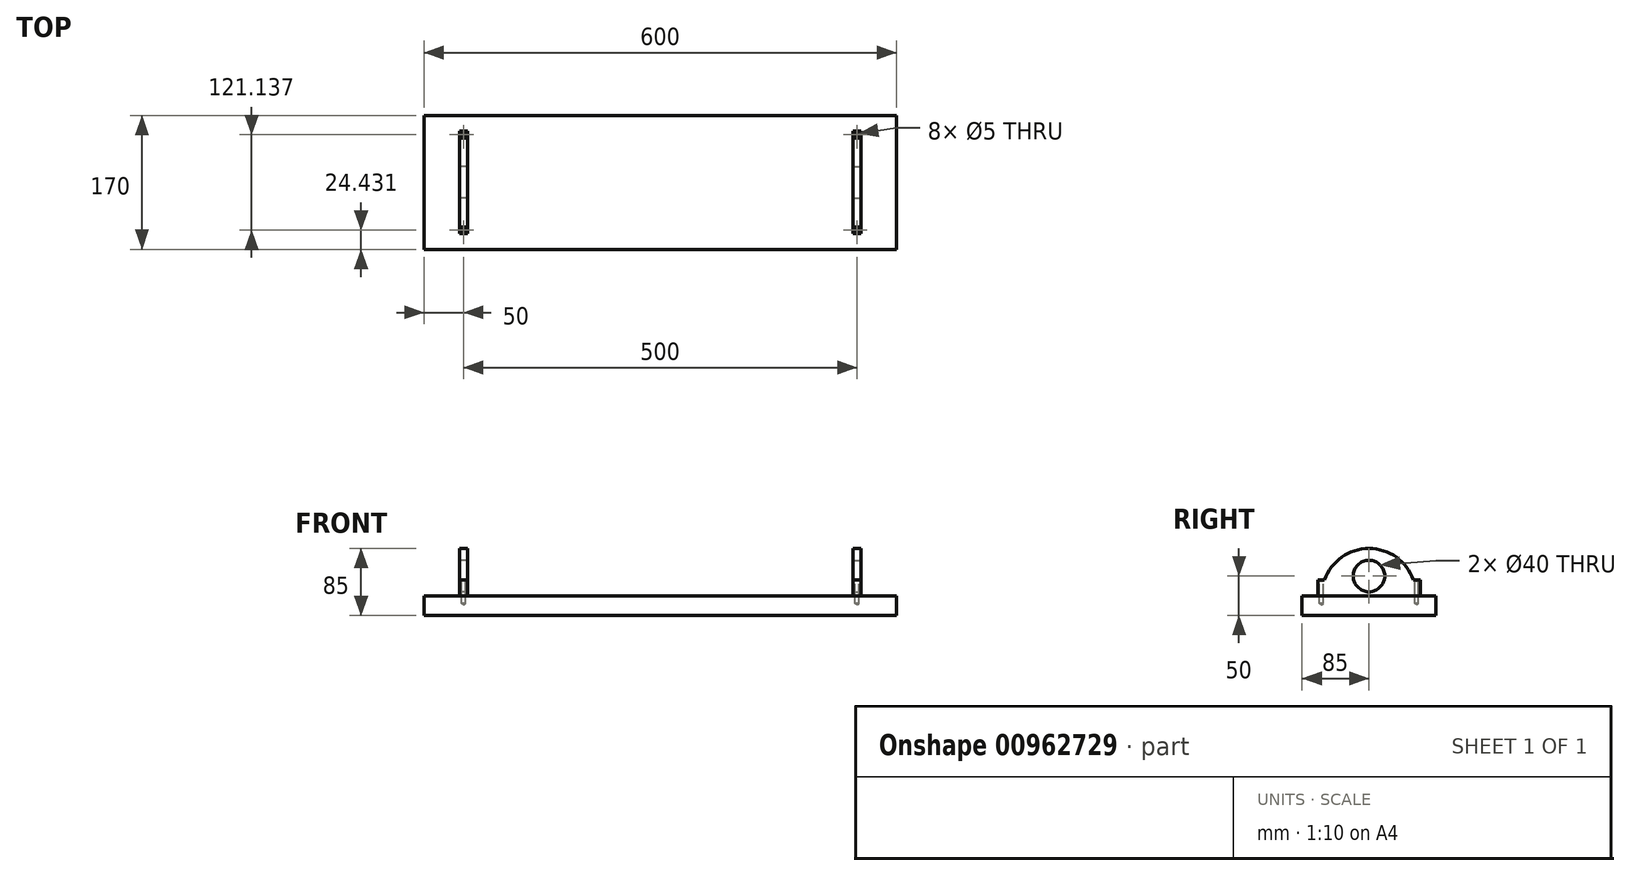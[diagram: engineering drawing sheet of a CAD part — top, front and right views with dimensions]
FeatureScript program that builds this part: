
annotation { "Feature Type Name" : "Feature", "Feature Type Description" : "" }
export const myFeature = defineFeature(function(context is Context, id is Id, definition is map)
    precondition{}
    {
        {
            var Q0;
            Q0=qCreatedBy(makeId("Top.planeOp"),FACE);
            var sketch = newSketch(context, id + "F0", { "sketchPlane" : qUnion([Q0])});
            skLineSegment(sketch, "E0.bottom", {"start": v(300, -85) * mm, "end": v(-300, -85) * mm});
            skLineSegment(sketch, "E0.top", {"start": v(300, 85) * mm, "end": v(-300, 85) * mm});
            skLineSegment(sketch, "E0.left", {"start": v(300, -85) * mm, "end": v(300, 85) * mm});
            skLineSegment(sketch, "E0.right", {"start": v(-300, -85) * mm, "end": v(-300, 85) * mm});
            skPoint(sketch, "E0.middle", {"position": v(0, 0) * mm});
            skSolve(sketch);
        }
        {
            var Q0;
            Q0=qSketchRegion(id+"F0",true);
            extrude(context, id + "F1", {"entities" : qUnion([Q0]), "depth" : 25 * mm, "offsetDistance" : 25 * mm});
        }
        {
            var Q0;
            Q0=qCreatedBy(makeId("Right.planeOp"),FACE);
            var sketch = newSketch(context, id + "F2", { "sketchPlane" : qUnion([Q0])});
            skLineSegment(sketch, "E1", {"start": v(65, 25) * mm, "end": v(65, 45) * mm});
            skLineSegment(sketch, "E2", {"start": v(65, 45) * mm, "end": v(56.57, 45) * mm});
            skLineSegment(sketch, "E3.MirrorCS", {"start": v(-65, 45) * mm, "end": v(-56.57, 45) * mm});
            skLineSegment(sketch, "E4.MirrorCS", {"start": v(-65, 25) * mm, "end": v(-65, 45) * mm});
            skLineSegment(sketch, "E5", {"start": v(65, 25) * mm, "end": v(-65, 25) * mm});
            skArc(sketch, "E6", {"start": v(56.57, 45) * mm, "mid": v(0, 85) * mm, "end": v(-56.57, 45) * mm});
            skSolve(sketch);
        }
        {
            var Q0;
            Q0=qSketchRegion(id+"F2",true);
            extrude(context, id + "F3", {"entities" : qUnion([Q0]), "endBound" : BoundingType.SYMMETRIC, "depth" : 10 * mm, "offsetDistance" : 25 * mm});
        }
        {
            var Q0;
            Q0=makeQuery(id+"F3.opExtrude","SWEPT_BODY",BODY,{"disambiguationData":[OSD([sQuery(id+"F2.wireOp",EDGE,"E1"),sQuery(id+"F2.wireOp",EDGE,"E2"),sQuery(id+"F2.wireOp",EDGE,"E3.MirrorCS"),sQuery(id+"F2.wireOp",EDGE,"E4.MirrorCS"),sQuery(id+"F2.wireOp",EDGE,"E5"),sQuery(id+"F2.wireOp",EDGE,"E6")])]});
            transform(context, id + "F4", {"entities" : qUnion([Q0]), "transformType" : TransformType.TRANSLATION_3D, "dx" : -250 * mm, "dy" : 0 * mm, "dz" : 0 * mm, "makeCopy" : true});
        }
        {
            var Q0;
            Q0=makeQuery(id+"F3.opExtrude","SWEPT_BODY",BODY,{"disambiguationData":[OSD([sQuery(id+"F2.wireOp",EDGE,"E1"),sQuery(id+"F2.wireOp",EDGE,"E2"),sQuery(id+"F2.wireOp",EDGE,"E3.MirrorCS"),sQuery(id+"F2.wireOp",EDGE,"E4.MirrorCS"),sQuery(id+"F2.wireOp",EDGE,"E5"),sQuery(id+"F2.wireOp",EDGE,"E6")])]});
            transform(context, id + "F5", {"entities" : qUnion([Q0]), "transformType" : TransformType.TRANSLATION_3D, "dx" : 250 * mm, "dy" : 0 * mm, "dz" : 0 * mm, "makeCopy" : false});
        }
        {
            var Q0;
            Q0=makeQuery(id+"F4.opPattern","COPY",FACE,{"derivedFrom":makeQuery(id+"F3.opExtrude","CAP_FACE",FACE,{"disambiguationData":[OSD([sQuery(id+"F2.wireOp",EDGE,"E1"),sQuery(id+"F2.wireOp",EDGE,"E2"),sQuery(id+"F2.wireOp",EDGE,"E3.MirrorCS"),sQuery(id+"F2.wireOp",EDGE,"E4.MirrorCS"),sQuery(id+"F2.wireOp",EDGE,"E5"),sQuery(id+"F2.wireOp",EDGE,"E6")])],"isStart":true}),"instanceName":"1"});
            var sketch = newSketch(context, id + "F6", { "sketchPlane" : qUnion([Q0])});
            skCircle(sketch, "E7", {"center": v(0, 50) * mm, "radius": 20 * mm});
            skSolve(sketch);
        }
        {
            var Q0;
            Q0=qSketchRegion(id+"F6",true);
            extrude(context, id + "F7", {"entities" : qUnion([Q0]), "operationType" : NewBodyOperationType.REMOVE, "oppositeDirection" : true, "depth" : 10 * mm, "offsetDistance" : 25 * mm});
        }
        {
            var Q0;
            Q0=makeQuery(id+"F3.opExtrude","CAP_FACE",FACE,{"disambiguationData":[OSD([sQuery(id+"F2.wireOp",EDGE,"E1"),sQuery(id+"F2.wireOp",EDGE,"E2"),sQuery(id+"F2.wireOp",EDGE,"E3.MirrorCS"),sQuery(id+"F2.wireOp",EDGE,"E4.MirrorCS"),sQuery(id+"F2.wireOp",EDGE,"E5"),sQuery(id+"F2.wireOp",EDGE,"E6")])],"isStart":false});
            var sketch = newSketch(context, id + "F8", { "sketchPlane" : qUnion([Q0])});
            skCircle(sketch, "E8", {"center": v(0, 50) * mm, "radius": 20 * mm});
            skSolve(sketch);
        }
        {
            var Q0;
            Q0=qSketchRegion(id+"F8",true);
            extrude(context, id + "F9", {"entities" : qUnion([Q0]), "operationType" : NewBodyOperationType.REMOVE, "oppositeDirection" : true, "depth" : 10 * mm, "offsetDistance" : 25 * mm});
        }
        {
            var Q0;
            Q0=makeQuery(id+"F4.opPattern","COPY",FACE,{"derivedFrom":makeQuery(id+"F3.opExtrude","SWEPT_FACE",FACE,{"disambiguationData":[OSD([sQuery(id+"F2.wireOp",EDGE,"E2")])]}),"instanceName":"1"});
            var sketch = newSketch(context, id + "F10", { "sketchPlane" : qUnion([Q0])});
            skPoint(sketch, "E9", {"position": v(-250, 60.57) * mm});
            skPoint(sketch, "E10.MirrorP", {"position": v(250, 60.57) * mm});
            skPoint(sketch, "E11.MirrorP", {"position": v(-250, -60.57) * mm});
            skPoint(sketch, "E12.MirrorP", {"position": v(250, -60.57) * mm});
            skCircle(sketch, "E13", {"center": v(-250, 60.57) * mm, "radius": 2.5 * mm});
            skCircle(sketch, "E14.MirrorC", {"center": v(-250, -60.57) * mm, "radius": 2.5 * mm});
            skCircle(sketch, "E15.MirrorC", {"center": v(250, 60.57) * mm, "radius": 2.5 * mm});
            skCircle(sketch, "E16.MirrorC", {"center": v(250, -60.57) * mm, "radius": 2.5 * mm});
            skSolve(sketch);
        }
        {
            var Q0;
            Q0=sQuery(id+"F10.wireOp",VERTEX,"E9");
            var Q1;
            Q1=sQuery(id+"F10.wireOp",VERTEX,"E11.MirrorP");
            var Q2;
            Q2=makeQuery(id+"F4.opPattern","COPY",BODY,{"derivedFrom":makeQuery(id+"F3.opExtrude","SWEPT_BODY",BODY,{"disambiguationData":[OSD([sQuery(id+"F2.wireOp",EDGE,"E1"),sQuery(id+"F2.wireOp",EDGE,"E2"),sQuery(id+"F2.wireOp",EDGE,"E3.MirrorCS"),sQuery(id+"F2.wireOp",EDGE,"E4.MirrorCS"),sQuery(id+"F2.wireOp",EDGE,"E5"),sQuery(id+"F2.wireOp",EDGE,"E6")])]}),"instanceName":"1"});
            var Q3;
            Q3=makeQuery(id+"F1.opExtrude","SWEPT_BODY",BODY,{"disambiguationData":[OSD([sQuery(id+"F0.wireOp",EDGE,"E0.bottom"),sQuery(id+"F0.wireOp",EDGE,"E0.top"),sQuery(id+"F0.wireOp",EDGE,"E0.left"),sQuery(id+"F0.wireOp",EDGE,"E0.right")])]});
            hole(context, id + "F11", {"style" : HoleStyle.C_SINK, "endStyle" : HoleEndStyle.BLIND, "holeDiameter" : 5 * mm, "cSinkDiameter" : 7 * mm, "cSinkAngle" : 90 * degree, "majorDiameter" : 5 * mm, "holeDepth" : 30 * mm, "isTappedThrough" : true, "tappedDepth" : 12 * mm, "tapClearance" : 3, "startFromSketch" : true, "locations" : qUnion([Q0, Q1]), "scope" : qUnion([Q2, Q3])});
        }
        {
            var Q0;
            Q0=makeQuery(id+"F4.opPattern","COPY",FACE,{"derivedFrom":makeQuery(id+"F3.opExtrude","SWEPT_FACE",FACE,{"disambiguationData":[OSD([sQuery(id+"F2.wireOp",EDGE,"E2")])]}),"instanceName":"1"});
            var sketch = newSketch(context, id + "F12", { "sketchPlane" : qUnion([Q0])});
            skCircle(sketch, "E17.0", {"center": v(-250, 60.57) * mm, "radius": 3.5 * mm});
            skSolve(sketch);
        }
        {
            var Q0;
            Q0=qSketchRegion(id+"F12",true);
            var Q1;
            Q1=makeQuery(id+"F1.opExtrude","CAP_FACE",FACE,{"disambiguationData":[OSD([sQuery(id+"F0.wireOp",EDGE,"E0.bottom"),sQuery(id+"F0.wireOp",EDGE,"E0.top"),sQuery(id+"F0.wireOp",EDGE,"E0.left"),sQuery(id+"F0.wireOp",EDGE,"E0.right")])],"isStart":true});
            extrude(context, id + "F13", {"entities" : qUnion([Q0]), "endBound" : BoundingType.UP_TO_SURFACE, "oppositeDirection" : true, "depth" : 25 * mm, "endBoundEntityFace" : qUnion([Q1]), "offsetDistance" : 25 * mm});
        }
        {
            var Q0;
            Q0=makeQuery(id+"F1.opExtrude","SWEPT_BODY",BODY,{"disambiguationData":[OSD([sQuery(id+"F0.wireOp",EDGE,"E0.bottom"),sQuery(id+"F0.wireOp",EDGE,"E0.top"),sQuery(id+"F0.wireOp",EDGE,"E0.left"),sQuery(id+"F0.wireOp",EDGE,"E0.right")])]});
            var Q1;
            Q1=makeQuery(id+"F4.opPattern","COPY",BODY,{"derivedFrom":makeQuery(id+"F3.opExtrude","SWEPT_BODY",BODY,{"disambiguationData":[OSD([sQuery(id+"F2.wireOp",EDGE,"E1"),sQuery(id+"F2.wireOp",EDGE,"E2"),sQuery(id+"F2.wireOp",EDGE,"E3.MirrorCS"),sQuery(id+"F2.wireOp",EDGE,"E4.MirrorCS"),sQuery(id+"F2.wireOp",EDGE,"E5"),sQuery(id+"F2.wireOp",EDGE,"E6")])]}),"instanceName":"1"});
            var Q2;
            Q2=makeQuery(id+"F13.opExtrude","SWEPT_BODY",BODY,{"disambiguationData":[OSD([sQuery(id+"F12.wireOp",EDGE,"E17.0")])]});
            booleanBodies(context, id + "F14", {"operationType" : BooleanOperationType.SUBTRACTION, "tools" : qUnion([Q0, Q1]), "targets" : qUnion([Q2]), "keepTools" : true});
        }
        {
            var Q0;
            Q0=makeQuery(id+"F3.opExtrude","SWEPT_FACE",FACE,{"disambiguationData":[OSD([sQuery(id+"F2.wireOp",EDGE,"E2")])]});
            var sketch = newSketch(context, id + "F15", { "sketchPlane" : qUnion([Q0])});
            skPoint(sketch, "E18", {"position": v(250, 60.57) * mm});
            skCircle(sketch, "E19", {"center": v(250, 60.57) * mm, "radius": 2.5 * mm});
            skCircle(sketch, "E20.MirrorC", {"center": v(250, -60.57) * mm, "radius": 2.5 * mm});
            skSolve(sketch);
        }
        {
            var Q0;
            Q0=sQuery(id+"F15.wireOp",VERTEX,"E18");
            var Q1;
            Q1=sQuery(id+"F15.wireOp",VERTEX,"E20.MirrorC.center");
            var Q2;
            Q2=makeQuery(id+"F3.opExtrude","SWEPT_BODY",BODY,{"disambiguationData":[OSD([sQuery(id+"F2.wireOp",EDGE,"E1"),sQuery(id+"F2.wireOp",EDGE,"E2"),sQuery(id+"F2.wireOp",EDGE,"E3.MirrorCS"),sQuery(id+"F2.wireOp",EDGE,"E4.MirrorCS"),sQuery(id+"F2.wireOp",EDGE,"E5"),sQuery(id+"F2.wireOp",EDGE,"E6")])]});
            var Q3;
            Q3=makeQuery(id+"F1.opExtrude","SWEPT_BODY",BODY,{"disambiguationData":[OSD([sQuery(id+"F0.wireOp",EDGE,"E0.bottom"),sQuery(id+"F0.wireOp",EDGE,"E0.top"),sQuery(id+"F0.wireOp",EDGE,"E0.left"),sQuery(id+"F0.wireOp",EDGE,"E0.right")])]});
            hole(context, id + "F16", {"style" : HoleStyle.C_SINK, "endStyle" : HoleEndStyle.BLIND, "holeDiameter" : 5 * mm, "cSinkDiameter" : 7 * mm, "cSinkAngle" : 90 * degree, "majorDiameter" : 5 * mm, "holeDepth" : 30 * mm, "isTappedThrough" : true, "tappedDepth" : 12 * mm, "tapClearance" : 3, "startFromSketch" : true, "locations" : qUnion([Q0, Q1]), "scope" : qUnion([Q2, Q3])});
        }
    });
